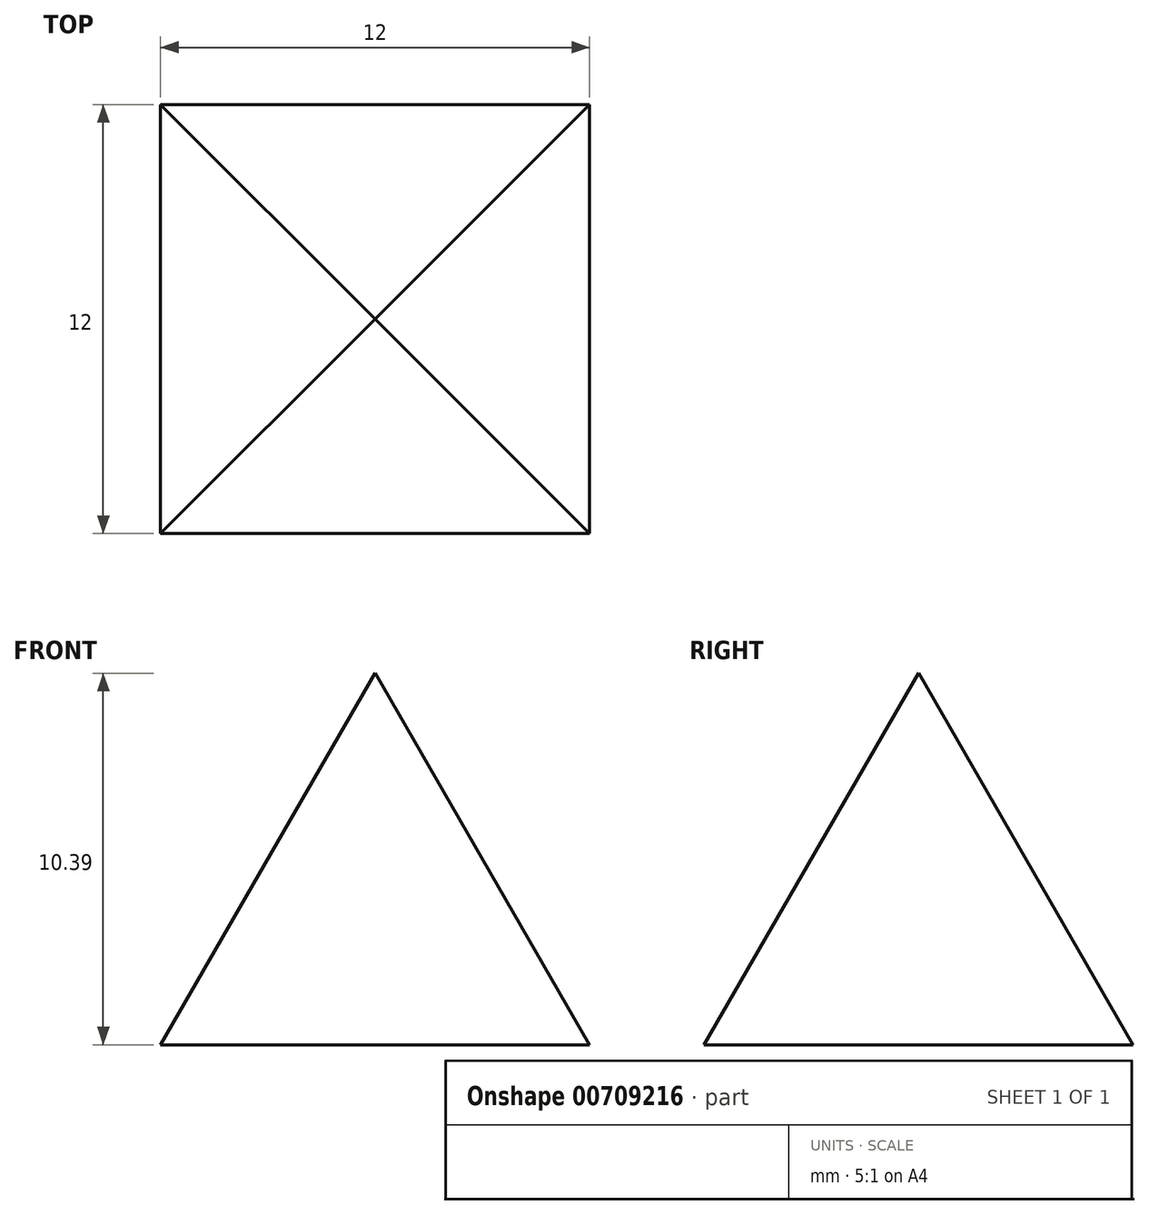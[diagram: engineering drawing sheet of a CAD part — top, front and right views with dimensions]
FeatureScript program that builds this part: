
annotation { "Feature Type Name" : "Feature", "Feature Type Description" : "" }
export const myFeature = defineFeature(function(context is Context, id is Id, definition is map)
    precondition{}
    {
        {
            var Q0;
            Q0=qCreatedBy(makeId("Top.planeOp"),FACE);
            var sketch = newSketch(context, id + "F0", { "sketchPlane" : qUnion([Q0])});
            skLineSegment(sketch, "E0.bottom", {"start": v(0, 0) * mm, "end": v(-12, 0) * mm});
            skLineSegment(sketch, "E0.top", {"start": v(0, 12) * mm, "end": v(-12, 12) * mm});
            skLineSegment(sketch, "E0.left", {"start": v(0, 0) * mm, "end": v(0, 12) * mm});
            skLineSegment(sketch, "E0.right", {"start": v(-12, 0) * mm, "end": v(-12, 12) * mm});
            skSolve(sketch);
        }
        {
            var Q0;
            Q0 = qSketchRegion(id + "F0", true);
            extrude(context, id + "F1", {"entities" : qUnion([Q0]), "depth" : 12 * mm, "offsetDistance" : 25.4 * mm, "hasDraft" : true, "draftAngle" : 30 * degree, "draftPullDirection" : true});
        }
    });
